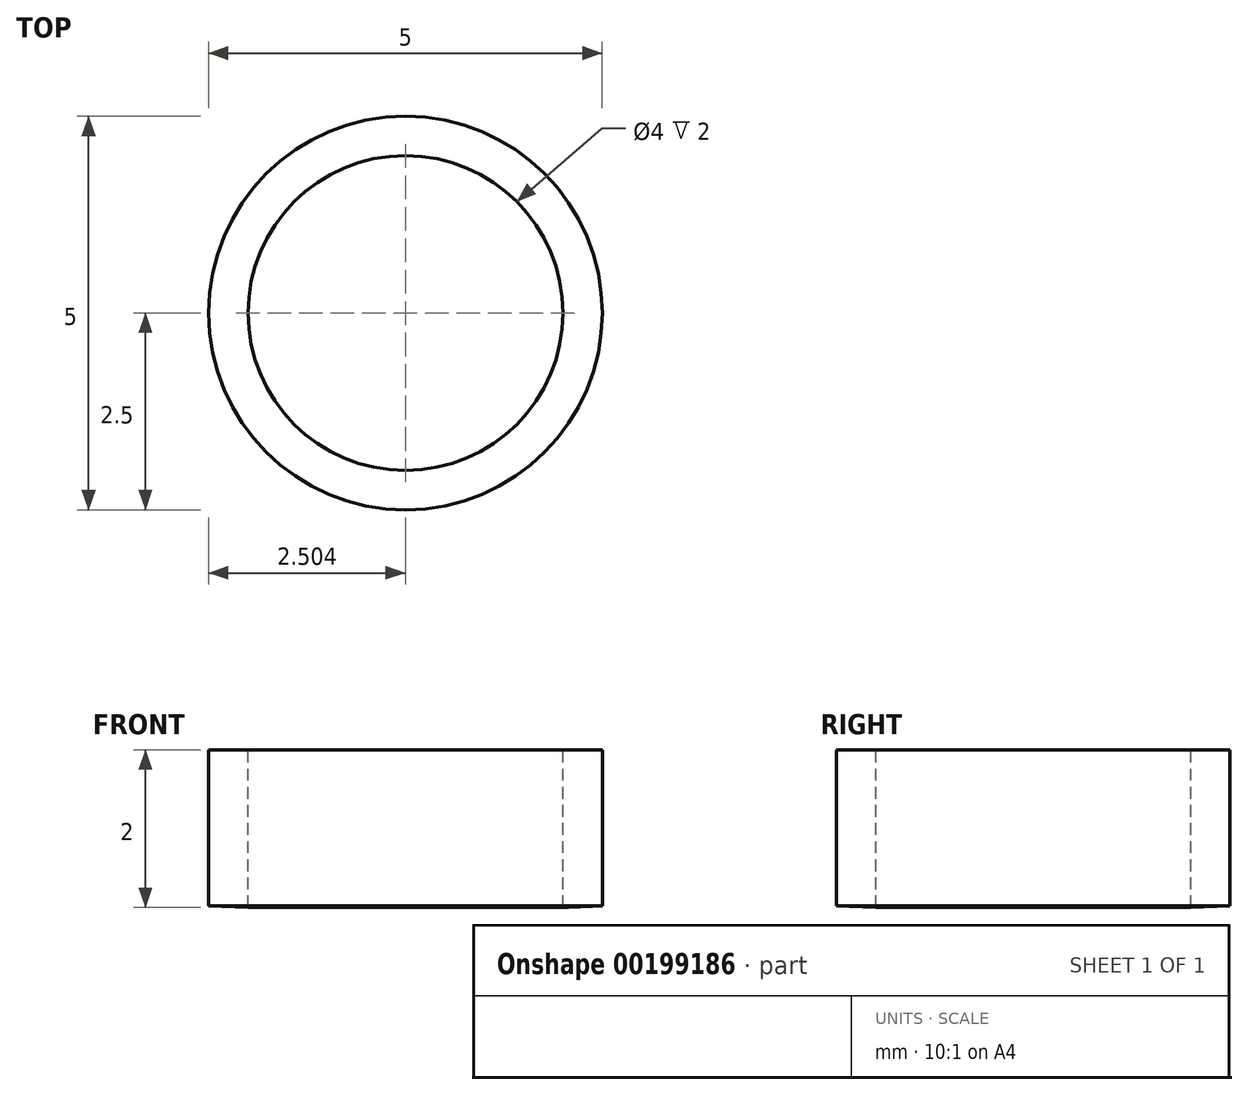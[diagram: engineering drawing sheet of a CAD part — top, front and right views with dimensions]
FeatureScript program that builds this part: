
annotation { "Feature Type Name" : "Feature", "Feature Type Description" : "" }
export const myFeature = defineFeature(function(context is Context, id is Id, definition is map)
    precondition{}
    {
        {
            var Q0;
            Q0=qCreatedBy(makeId("Front.planeOp"),FACE);
            var sketch = newSketch(context, id + "F0", { "sketchPlane" : qUnion([Q0])});
            skLineSegment(sketch, "E0", {"start": v(-15.09, 1.98) * mm, "end": v(-15.09, -0.02) * mm});
            skLineSegment(sketch, "E1", {"start": v(-13.09, -0.02) * mm, "end": v(-13.09, 1.98) * mm});
            skLineSegment(sketch, "E2", {"start": v(-13.09, 1.98) * mm, "end": v(-12.59, 1.98) * mm});
            skLineSegment(sketch, "E3", {"start": v(-12.59, 1.98) * mm, "end": v(-12.59, 0) * mm});
            skLineSegment(sketch, "E4", {"start": v(-12.59, 0) * mm, "end": v(-13.09, -0.02) * mm});
            skSolve(sketch);
        }
        {
            var Q0;
            Q0=makeQuery(id+"F0.imprint","IMPRINT",FACE,{"disambiguationData":[TD([[makeQuery(id+"F0.imprint","IMPRINT",EDGE,{"derivedFrom":sQuery(id+"F0.wireOp",EDGE,"E1")}),-1.0]])]});
            var Q1;
            Q1=sQuery(id+"F0.wireOp",EDGE,"E0");
            revolve(context, id + "F1", {"entities" : qUnion([Q0]), "axis" : qUnion([Q1]), "revolveType" : RevolveType.FULL});
        }
    });
